# Revit family: FU_Table_Sandler_Toffee 4-0
name_source: partatom
category: Furniture
units: mm (PartAtom-declared; Revit-internal decimal feet)

## family parameters
Always vertical = Yes
Cut with Voids When Loaded = No
OmniClass Number = 23.40.20.00
OmniClass Title = General Furniture and Specialties
Room Calculation Point = No
Shared = No
Work Plane-Based = No

## types (1)
- Toffee 4.0
    Default Elevation = 0 mm  [stored 0 ft]
    Depth = 400 mm  [stored 1.31234 ft]
    Description = Solid beech high table with shelf and detailing at the top of legs.
    Frame = Wood - Beech - White Aniline
    Height = 850 mm  [stored 2.78871 ft]
    Manufacturer = Sandler
    Model = Toffee 4.0
    URL = https://www.sandlerseating.com
    Width = 1300 mm  [stored 4.26509 ft]

note: [stored X ft] marks values corroborated as IEEE doubles in the binary element streams (Revit-internal decimal feet)

## geometry (parser evidence)
native form markers: Sweep x1
no freeform markers — native parametric forms only
